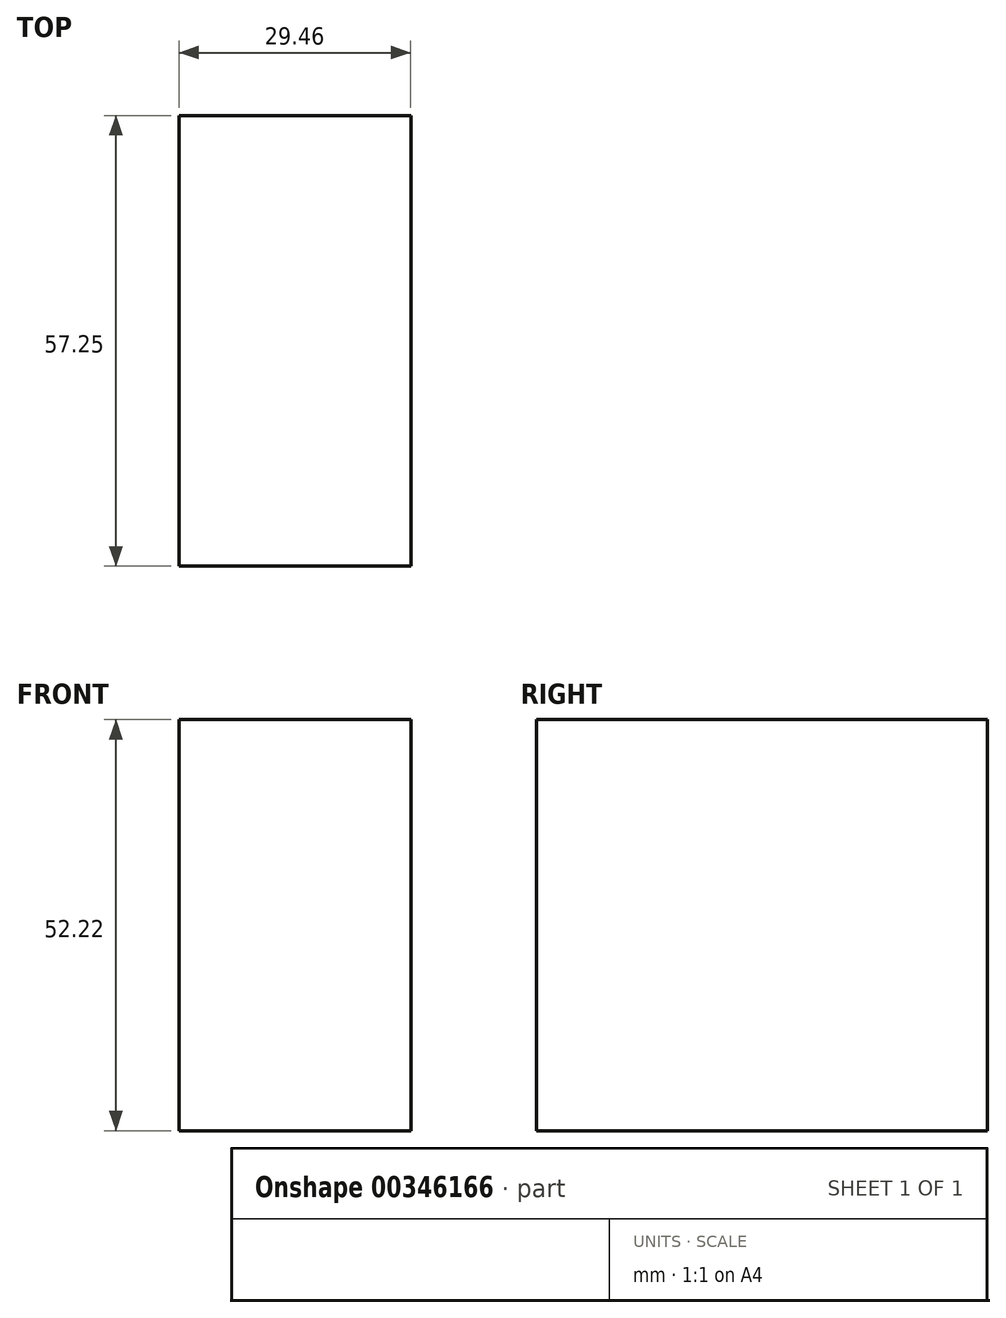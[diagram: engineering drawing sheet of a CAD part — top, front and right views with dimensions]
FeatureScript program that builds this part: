
annotation { "Feature Type Name" : "Feature", "Feature Type Description" : "" }
export const myFeature = defineFeature(function(context is Context, id is Id, definition is map)
    precondition{}
    {
        {
            var Q0;
            Q0=qCreatedBy(makeId("Right.planeOp"),FACE);
            var sketch = newSketch(context, id + "F0", { "sketchPlane" : qUnion([Q0])});
            skLineSegment(sketch, "E0.bottom", {"start": v(25.8, 24.54) * mm, "end": v(-31.46, 24.54) * mm});
            skLineSegment(sketch, "E0.top", {"start": v(25.8, -27.68) * mm, "end": v(-31.46, -27.68) * mm});
            skLineSegment(sketch, "E0.left", {"start": v(25.8, 24.54) * mm, "end": v(25.8, -27.68) * mm});
            skLineSegment(sketch, "E0.right", {"start": v(-31.46, 24.54) * mm, "end": v(-31.46, -27.68) * mm});
            skSolve(sketch);
        }
        {
            var Q0;
            Q0=makeQuery(id+"F0.imprint","IMPRINT",FACE,{"disambiguationData":[TD([[makeQuery(id+"F0.imprint","IMPRINT",EDGE,{"derivedFrom":sQuery(id+"F0.wireOp",EDGE,"E0.bottom")}),1.0]])]});
            extrude(context, id + "F1", {"entities" : qUnion([Q0]), "depth" : 29.46 * mm});
        }
    });
